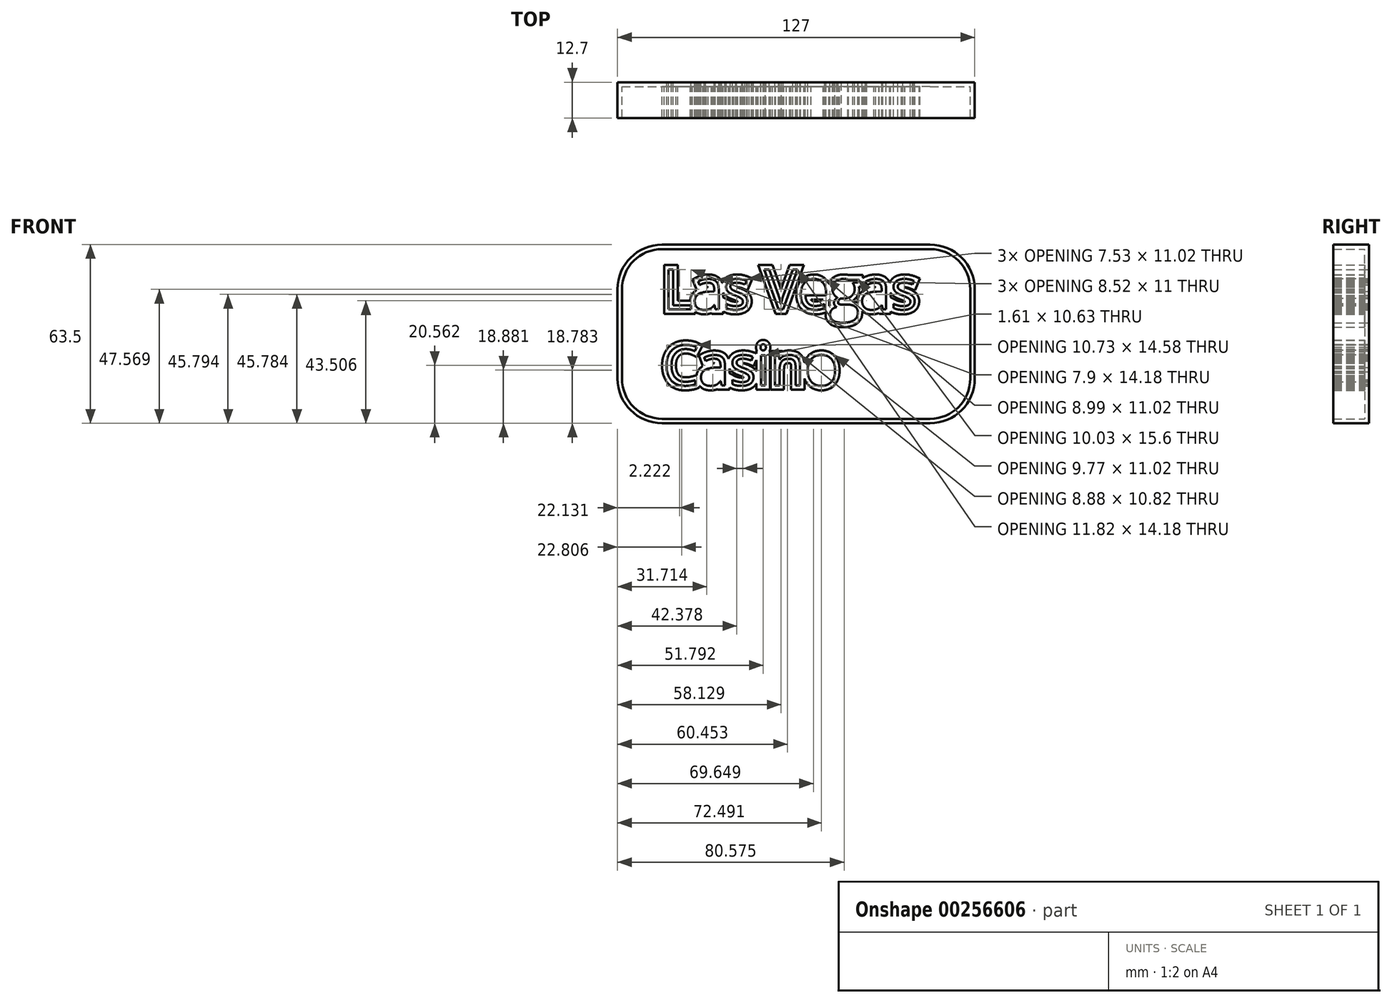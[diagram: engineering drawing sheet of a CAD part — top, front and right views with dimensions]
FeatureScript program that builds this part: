
annotation { "Feature Type Name" : "Feature", "Feature Type Description" : "" }
export const myFeature = defineFeature(function(context is Context, id is Id, definition is map)
    precondition{}
    {
        {
            var Q0;
            Q0=qCreatedBy(makeId("Front.planeOp"),FACE);
            var sketch = newSketch(context, id + "F0", { "sketchPlane" : qUnion([Q0])});
            skLineSegment(sketch, "E0.bottom", {"start": v(47.62, 31.75) * mm, "end": v(-47.63, 31.75) * mm});
            skLineSegment(sketch, "E0.top", {"start": v(47.62, -31.75) * mm, "end": v(-47.63, -31.75) * mm});
            skLineSegment(sketch, "E0.left", {"start": v(63.5, 15.88) * mm, "end": v(63.5, -15.87) * mm});
            skLineSegment(sketch, "E0.right", {"start": v(-63.5, 15.88) * mm, "end": v(-63.5, -15.88) * mm});
            skPoint(sketch, "E0.middle", {"position": v(0, 0) * mm});
            skPoint(sketch, "E1.visualSharp", {"position": v(-63.5, 31.75) * mm});
            skArc(sketch, "E1.filletArc", {"start": v(-47.63, 31.75) * mm, "mid": v(-58.85, 27.1) * mm, "end": v(-63.5, 15.88) * mm});
            skPoint(sketch, "E2.visualSharp", {"position": v(-63.5, -31.75) * mm});
            skArc(sketch, "E2.filletArc", {"start": v(-63.5, -15.88) * mm, "mid": v(-58.85, -27.1) * mm, "end": v(-47.63, -31.75) * mm});
            skPoint(sketch, "E3.visualSharp", {"position": v(63.5, -31.75) * mm});
            skArc(sketch, "E3.filletArc", {"start": v(47.62, -31.75) * mm, "mid": v(58.85, -27.1) * mm, "end": v(63.5, -15.87) * mm});
            skPoint(sketch, "E4.visualSharp", {"position": v(63.5, 31.75) * mm});
            skArc(sketch, "E4.filletArc", {"start": v(63.5, 15.88) * mm, "mid": v(58.85, 27.1) * mm, "end": v(47.62, 31.75) * mm});
            skText(sketch, "E5", { "text": "Las Vegas \nCasino", "fontName": "OpenSans-Regular.ttf"});
            const initialGuessF0  = {"E5": [-0.04727, 0.00873, 1, 0, 0.0143]};
            skSetInitialGuess(sketch, initialGuessF0);
            skSolve(sketch);
        }
        {
            var Q0;
            Q0 = qSketchRegion(id + "F0", true);
            extrude(context, id + "F1", {"entities" : qUnion([Q0]), "depth" : 12.7 * mm});
        }
        {
            var Q0;
            Q0=makeQuery(id+"F1.opExtrude","CAP_FACE",FACE,{"disambiguationData":[OSD([sQuery(id+"F0.wireOp",EDGE,"E0.bottom"),sQuery(id+"F0.wireOp",EDGE,"E0.top"),sQuery(id+"F0.wireOp",EDGE,"E0.left"),sQuery(id+"F0.wireOp",EDGE,"E0.right"),sQuery(id+"F0.wireOp",EDGE,"E1.filletArc"),sQuery(id+"F0.wireOp",EDGE,"E2.filletArc"),sQuery(id+"F0.wireOp",EDGE,"E3.filletArc"),sQuery(id+"F0.wireOp",EDGE,"E4.filletArc")])],"isStart":false});
            shell(context, id + "F2", {"entities" : qUnion([Q0]), "thickness" : 1.59 * mm});
        }
    });
